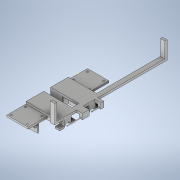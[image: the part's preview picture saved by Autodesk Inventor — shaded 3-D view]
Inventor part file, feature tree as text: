
AUTODESK INVENTOR PART (.ipt)
format: ipt  version: 2020.2 (Build 242310000, 310)  size: 752,128 bytes
history: native  units: mm
features: sketch x33, extrude x33, projected_geometry x12, hole x3
ambient origin geometry x8: Origin, YZ Plane, XZ Plane, XY Plane, X Axis, Y Axis, Z Axis, Center Point
bodies: Solid1 (feature_tree)
feature tree (81):
  sketch  "Sketch1"  dims[d0=8.0mm d1=98.298mm]
  extrude  "Extrusion1"  Depth=98.298mm
  extrude  "Extrusion2"  Depth=4.0mm
  extrude  "Extrusion3"  Depth=4.0mm TaperAngle=0.0deg
  extrude  "Extrusion4"  Depth=34.0mm
  extrude  "Extrusion5"  Depth=12.7mm
  extrude  "Extrusion6"  Depth=25.0mm
  hole  "Hole1"  [1 undecoded]
  extrude  "Extrusion11"  TaperAngle=60.0deg  [1 undecoded]
  extrude  "Extrusion12"  TaperAngle=120.0deg  [1 undecoded]
  sketch  "Sketch16"  dims[d19=6.4262mm d20=120.0deg]
  extrude  "Extrusion13"  Depth=6.4262mm
  extrude  "Extrusion14"  Depth=6.4262mm
  sketch  "Sketch17"  dims[d21=120.0deg d22=6.4262mm]
  extrude  "Extrusion15"  Depth=25.4mm TaperAngle=0.0deg
  extrude  "Extrusion18"  Depth=6.0mm
  extrude  "Extrusion19"  Depth=8.89mm
  extrude  "Extrusion20"  Depth=10.0mm
  hole  "Hole2"  [1 undecoded]
  extrude  "Extrusion21"  Depth=2.0mm
  extrude  "Extrusion22"  Depth=2.0mm
  sketch  "Sketch27"  dims[d45=8.89mm d46=2.0mm]
  extrude  "Extrusion23"  Depth=25.4mm
  extrude  "Extrusion24"  Depth=32.48mm
  extrude  "Extrusion25"  TaperAngle=90.0deg  [1 undecoded]
  sketch  "Sketch29"  dims[d79=51.53mm d80=32.48mm]
  extrude  "Extrusion26"  Depth=2.0mm
  extrude  "Extrusion27"  Depth=21.0mm
  extrude  "Extrusion28"  Depth=36.0mm TaperAngle=0.0deg
  extrude  "Extrusion29"  Depth=8.0mm
  extrude  "Extrusion30"  Depth=17.5mm
  extrude  "Extrusion32"  Depth=35.0mm
  extrude  "Extrusion33"  Depth=5.0mm
  extrude  "Extrusion34"  TaperAngle=90.0deg  [1 undecoded]
  extrude  "Extrusion35"  Depth=5.0mm
  extrude  "Extrusion38"  Depth=25.4mm TaperAngle=0.0deg
  extrude  "Extrusion39"  Depth=1.5mm
  extrude  "Extrusion40"  TaperAngle=0.0deg  [1 undecoded]
  hole  "Hole4"  [1 undecoded]
  extrude  "Extrusion43"  Depth=28.8036mm
  extrude  "Extrusion44"  Depth=25.4mm TaperAngle=0.0deg
  sketch  "Sketch2"  dims[d2=8.0mm d3=4.0mm]
  sketch  "Sketch3"  dims[d4=4.0mm d5=4.0mm d6=0.0mm]
  sketch  "Sketch4"  dims[d7=34.0mm d8=0.0mm d9=19.558mm]
  sketch  "Sketch5"  dims[d10=16.1125mm d11=12.7mm]
  sketch  "Sketch6"  dims[d12=25.0mm d13=0.0mm d14=11.1125mm]
  sketch  "Sketch14"  dims[d15=6.4135mm d16=12.827mm]
  projected_geometry  "Projected Loop2"
  sketch  "Sketch15"  dims[d17=6.4262mm d18=60.0deg]
  projected_geometry  "Projected Loop3"
  sketch  "Sketch18"  dims[d23=120.0deg d24=6.4262mm]
  sketch  "Sketch21"  dims[d25=120.0deg d26=25.4mm d27=0.0mm]
  sketch  "Sketch22"  dims[d28=6.0mm d29=8.89mm]
  sketch  "Sketch23"  dims[d30=5.9944mm d31=8.89mm]
  sketch  "Sketch24"  dims[d32=25.4mm d33=0.0mm d34=10.0mm]
  sketch  "Sketch25"  dims[d35=90.0deg d36=20.0mm]
  projected_geometry  "Projected Loop5"
  sketch  "Sketch26"  dims[d37=3.4mm d38=19.05mm d39=6.2992mm d40=6.35mm d41=90.0deg d42=5.0mm d43=0.0mm d44=2.0mm]
  sketch  "Sketch28"  dims[d47=25.4mm d48=0.0mm d78=16.24mm]
  sketch  "Sketch30"  dims[d81=90.0deg d82=90.0deg]
  sketch  "Sketch32"  dims[d83=4.0mm d84=0.0mm d87=2.0mm]
  projected_geometry  "Projected Loop6"
  sketch  "Sketch33"  dims[d88=2.0mm d89=21.0mm]
  projected_geometry  "Projected Loop7"
  sketch  "Sketch35"  dims[d90=2.0mm d91=36.0mm d92=0.0mm]
  projected_geometry  "Projected Loop8"
  sketch  "Sketch36"  dims[d93=13.878mm d94=8.0mm]
  sketch  "Sketch37"  dims[d95=180.0deg d96=17.5mm]
  sketch  "Sketch38"  dims[d97=90.0deg d98=35.0mm]
  sketch  "Sketch42"  dims[d99=3.5mm d100=5.0mm]
  sketch  "Sketch43"  dims[d101=7.0mm d102=90.0deg]
  projected_geometry  "Projected Loop9"
  projected_geometry  "Projected Loop10"
  projected_geometry  "Projected Loop11"
  projected_geometry  "Projected Loop12"
  sketch  "Sketch44"  dims[d103=5.0mm d104=3.4mm]
  sketch  "Sketch45"  dims[d105=3.4mm d106=25.4mm d107=0.0mm]
  sketch  "Sketch48"  dims[d108=6.4262mm d109=0.0mm d110=1.5mm]
  sketch  "Sketch49"  dims[d111=1.5mm d112=0.0mm d113=0.0mm d128=44.8mm d129=28.8036mm d130=25.4mm d131=0.0mm d132=3.2131mm d133=6.4262mm d134=120.0deg d135=3.2131mm d136=6.4262mm d137=120.0deg d138=25.4mm d139=0.0mm d140=8.001mm d141=13.8938mm d142=8.001mm d143=0.0mm d144=25.4mm d145=0.0mm d146=10.0mm d147=20.0mm d148=3.4mm d149=19.05mm d150=6.2992mm d151=6.35mm d152=90.0deg d153=5.0mm d154=0.0mm d155=16.2433mm d156=32.4866mm d157=51.5366mm d158=4.0mm d159=0.0mm d160=21.0mm d161=2.0mm d162=2.0mm d163=2.0mm d164=2.0mm d165=36.0mm d166=0.0mm d167=7.0mm d168=5.0mm d169=5.0mm d170=17.5mm d171=35.0mm d172=3.4mm d173=3.4mm d174=5.0mm d175=0.0mm d176=5.0mm d177=0.0mm d178=1.5mm d179=1.5mm d180=25.4mm d181=0.0mm d182=19.05mm d183=10.0mm d184=5.08mm d185=4.0mm d186=0.0mm d187=10.0mm d188=0.0mm d189=2.0mm d190=2.0mm d191=25.4mm d192=0.0mm d194=30.0mm d195=0.0mm d196=99.06mm d197=0.0mm d201=11.43mm d202=0.0mm d203=25.4mm d204=0.0mm d205=25.4mm d206=0.0mm d207=25.4mm d208=0.0mm d239=25.4mm d240=0.0mm d241=1.5mm d242=0.0mm d243=39.0mm d244=35.0mm d245=39.0mm d246=35.0mm d247=3.0mm d248=0.0mm d249=5.0mm d250=5.0mm d251=29.7mm d252=26.05mm d253=4.0mm d254=4.0mm d255=29.7mm d256=26.05mm d257=3.4mm d258=19.05mm d259=6.2992mm d260=6.35mm d261=90.0deg d262=25.4mm d263=20.594885mm d271=4.0mm d272=28.4mm d273=0.0mm d274=25.4mm d275=0.0mm d214=12.7mm d215=0.872665mm d216=12.7mm d217=0.872665mm d228=12.7mm d229=0.872665mm d230=12.7mm d231=0.872665mm]
  projected_geometry  "Projected Loop13"
  projected_geometry  "Projected Loop14"
note: 8 required parameter values undecoded (feature->parameter linkage not recoverable at this tier; creation-order binding heuristic only, values carry confidence <= 0.55)
